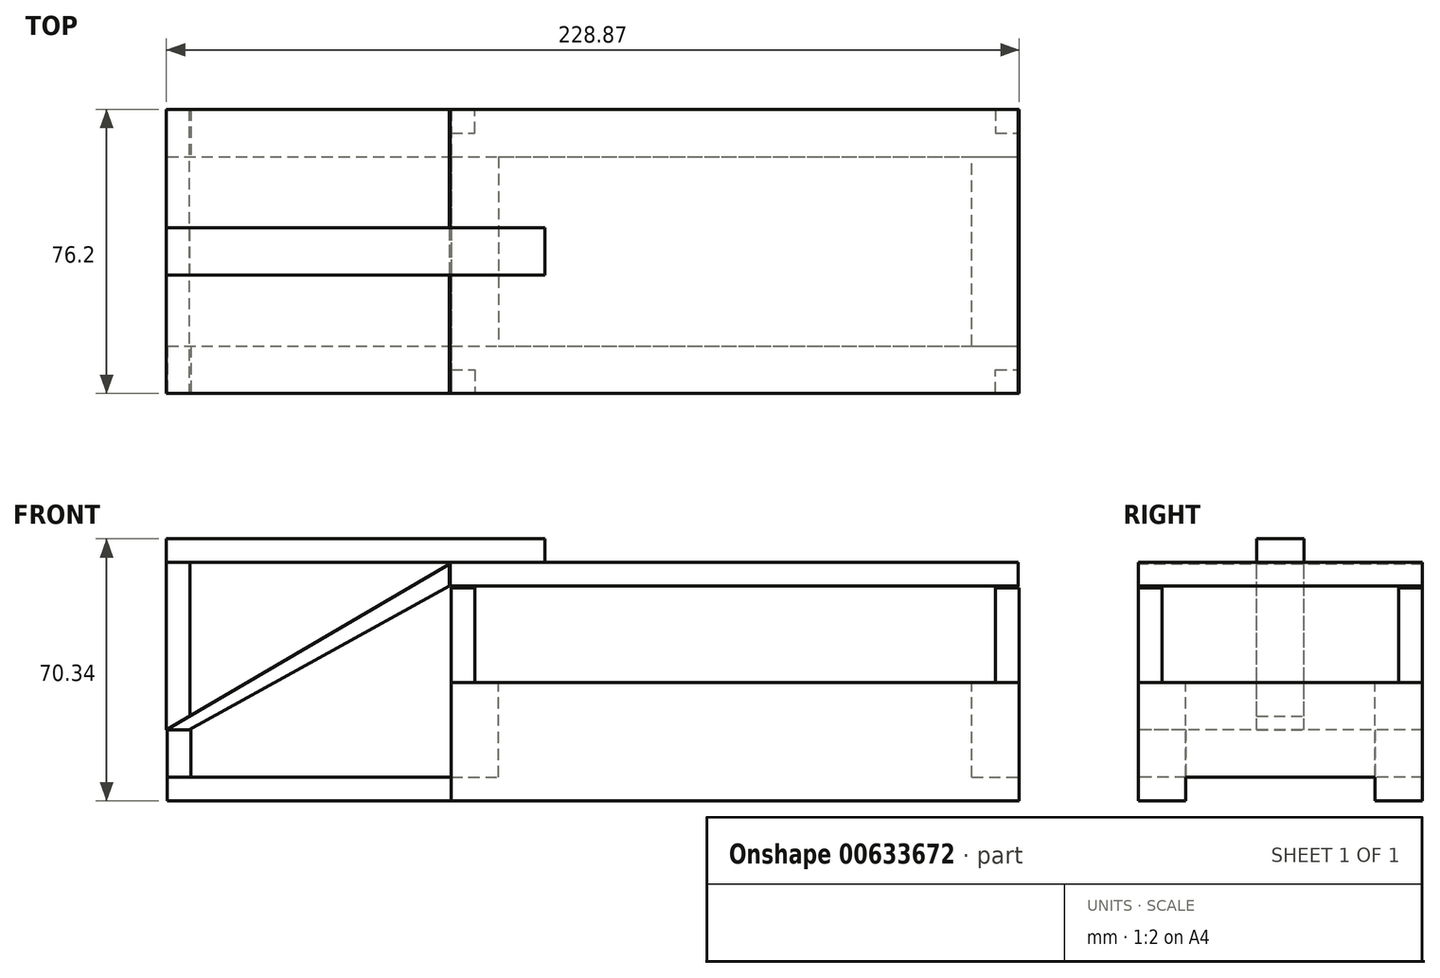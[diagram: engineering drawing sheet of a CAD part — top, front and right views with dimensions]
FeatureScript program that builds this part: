
annotation { "Feature Type Name" : "Feature", "Feature Type Description" : "" }
export const myFeature = defineFeature(function(context is Context, id is Id, definition is map)
    precondition{}
    {
        {
            var Q0;
            Q0=qCreatedBy(makeId("Front.planeOp"),FACE);
            var sketch = newSketch(context, id + "F0", { "sketchPlane" : qUnion([Q0])});
            skLineSegment(sketch, "E0", {"start": v(-114.8, -72) * mm, "end": v(37.6, -72) * mm});
            skLineSegment(sketch, "E1", {"start": v(37.6, -72) * mm, "end": v(37.6, -40.25) * mm});
            skLineSegment(sketch, "E2", {"start": v(37.6, -40.25) * mm, "end": v(-114.8, -40.25) * mm});
            skLineSegment(sketch, "E3", {"start": v(-114.8, -40.25) * mm, "end": v(-114.8, -72) * mm});
            skLineSegment(sketch, "E4", {"start": v(-114.8, -65.65) * mm, "end": v(37.6, -65.65) * mm});
            skSolve(sketch);
        }
        {
            var Q0;
            Q0 = qSketchRegion(id + "F0", true);
            extrude(context, id + "F1", {"entities" : qUnion([Q0]), "oppositeDirection" : true, "depth" : 76.2 * mm, "offsetDistance" : 25.4 * mm});
        }
        {
            var Q0;
            Q0=makeQuery(id+"F1.opExtrude","SWEPT_FACE",FACE,{"disambiguationData":[OSD([sQuery(id+"F0.wireOp",EDGE,"E2")])]});
            var sketch = newSketch(context, id + "F2", { "sketchPlane" : qUnion([Q0])});
            skLineSegment(sketch, "E5", {"start": v(-114.8, 69.85) * mm, "end": v(-108.44, 69.85) * mm});
            skLineSegment(sketch, "E6", {"start": v(-108.44, 69.85) * mm, "end": v(-108.44, 76.2) * mm});
            skLineSegment(sketch, "E7", {"start": v(-114.8, 6.35) * mm, "end": v(-108.44, 6.35) * mm});
            skLineSegment(sketch, "E8", {"start": v(-108.44, 6.35) * mm, "end": v(-108.44, 0) * mm});
            skLineSegment(sketch, "E9", {"start": v(31.26, 76.2) * mm, "end": v(31.26, 69.85) * mm});
            skLineSegment(sketch, "E10", {"start": v(31.26, 69.85) * mm, "end": v(37.6, 69.85) * mm});
            skLineSegment(sketch, "E11", {"start": v(31.26, 0) * mm, "end": v(31.26, 6.35) * mm});
            skLineSegment(sketch, "E12", {"start": v(31.26, 6.35) * mm, "end": v(37.6, 6.35) * mm});
            skSolve(sketch);
        }
        {
            var Q0;
            Q0 = qSketchRegion(id + "F2", true);
            var Q1;
            {var subQ0=sQuery(id+"F2.wireOp",EDGE,"E5");Q1=makeQuery(id+"F2.imprint","IMPRINT",FACE,{"disambiguationData":[TD([[makeQuery(id+"F2.imprint","IMPRINT",EDGE,{"derivedFrom":subQ0}),1.0]])]});}
            extrude(context, id + "F3", {"entities" : qUnion([Q0, Q1]), "depth" : 25.4 * mm, "offsetDistance" : 25.4 * mm});
        }
        {
            var Q0;
            {var subQ0=sQuery(id+"F2.wireOp",EDGE,"E7");Q0=makeQuery(id+"F2.imprint","IMPRINT",FACE,{"disambiguationData":[TD([[makeQuery(id+"F2.imprint","IMPRINT",EDGE,{"derivedFrom":subQ0}),-1.0]])]});}
            extrude(context, id + "F4", {"entities" : qUnion([Q0]), "depth" : 25.4 * mm, "offsetDistance" : 25.4 * mm});
        }
        {
            var Q0;
            {var subQ0=sQuery(id+"F2.wireOp",EDGE,"E11");Q0=makeQuery(id+"F2.imprint","IMPRINT",FACE,{"disambiguationData":[TD([[makeQuery(id+"F2.imprint","IMPRINT",EDGE,{"derivedFrom":subQ0}),-1.0]])]});}
            extrude(context, id + "F5", {"entities" : qUnion([Q0]), "depth" : 25.4 * mm, "offsetDistance" : 25.4 * mm});
        }
        {
            var Q0;
            {var subQ0=sQuery(id+"F2.wireOp",EDGE,"E9");Q0=makeQuery(id+"F2.imprint","IMPRINT",FACE,{"disambiguationData":[TD([[makeQuery(id+"F2.imprint","IMPRINT",EDGE,{"derivedFrom":subQ0}),1.0]])]});}
            extrude(context, id + "F6", {"entities" : qUnion([Q0]), "depth" : 25.4 * mm, "offsetDistance" : 25.4 * mm});
        }
        {
            var Q0;
            {var subQ0=sQuery(id+"F0.wireOp",EDGE,"E2");var subQ1=sQuery(id+"F0.wireOp",EDGE,"E1");Q0=makeQuery(id+"F6.boolean.opBoolean","MERGE",FACE,{"derivedFrom":[makeQuery(id+"F5.boolean.opBoolean","MERGE",FACE,{"derivedFrom":[makeQuery(id+"F1.opExtrude","SWEPT_FACE",FACE,{"disambiguationData":[OSD([subQ1])]}),makeQuery(id+"F5.opExtrude","SWEPT_FACE",FACE,{"disambiguationData":[OSD([subQ1,subQ0])]})]}),makeQuery(id+"F6.opExtrude","SWEPT_FACE",FACE,{"disambiguationData":[OSD([subQ1,subQ0])]})]});}
            var sketch = newSketch(context, id + "F7", { "sketchPlane" : qUnion([Q0])});
            skLineSegment(sketch, "E13", {"start": v(12.7, -72) * mm, "end": v(12.7, -65.65) * mm});
            skLineSegment(sketch, "E14", {"start": v(12.7, -65.65) * mm, "end": v(63.5, -65.65) * mm});
            skLineSegment(sketch, "E15", {"start": v(63.5, -65.65) * mm, "end": v(63.5, -72) * mm});
            skSolve(sketch);
        }
        {
            var Q0;
            Q0 = qSketchRegion(id + "F7", true);
            var Q1;
            {var subQ0=sQuery(id+"F7.wireOp",EDGE,"E13");Q1=makeQuery(id+"F7.imprint","IMPRINT",FACE,{"disambiguationData":[TD([[makeQuery(id+"F7.imprint","IMPRINT",EDGE,{"derivedFrom":subQ0}),-1.0]])]});}
            extrude(context, id + "F8", {"entities" : qUnion([Q0, Q1]), "operationType" : NewBodyOperationType.REMOVE, "oppositeDirection" : true, "depth" : 155.96 * mm, "offsetDistance" : 25.4 * mm});
        }
        {
            var Q0;
            Q0=makeQuery(id+"F1.opExtrude","SWEPT_FACE",FACE,{"disambiguationData":[OSD([sQuery(id+"F0.wireOp",EDGE,"E2")])]});
            var sketch = newSketch(context, id + "F9", { "sketchPlane" : qUnion([Q0])});
            skLineSegment(sketch, "E16", {"start": v(-102.1, 63.5) * mm, "end": v(-102.1, 12.7) * mm});
            skLineSegment(sketch, "E17", {"start": v(-102.1, 12.7) * mm, "end": v(24.9, 12.7) * mm});
            skLineSegment(sketch, "E18", {"start": v(24.9, 12.7) * mm, "end": v(24.9, 63.5) * mm});
            skLineSegment(sketch, "E19", {"start": v(-102.1, 63.5) * mm, "end": v(24.9, 63.5) * mm});
            skSolve(sketch);
        }
        {
            var Q0;
            Q0 = qSketchRegion(id + "F9", true);
            extrude(context, id + "F10", {"entities" : qUnion([Q0]), "operationType" : NewBodyOperationType.REMOVE, "oppositeDirection" : true, "depth" : 44.7 * mm, "offsetDistance" : 25.4 * mm});
        }
        {
            var Q0;
            Q0=qCreatedBy(makeId("Front.planeOp"),FACE);
            var sketch = newSketch(context, id + "F11", { "sketchPlane" : qUnion([Q0])});
            skLineSegment(sketch, "E20", {"start": v(-115.05, -14.36) * mm, "end": v(37.35, -14.36) * mm});
            skLineSegment(sketch, "E21", {"start": v(37.35, -14.36) * mm, "end": v(37.35, -8) * mm});
            skLineSegment(sketch, "E22", {"start": v(37.35, -8) * mm, "end": v(-115.05, -8) * mm});
            skLineSegment(sketch, "E23", {"start": v(-115.05, -8) * mm, "end": v(-115.05, -14.36) * mm});
            skSolve(sketch);
        }
        {
            var Q0;
            Q0 = qSketchRegion(id + "F11", true);
            extrude(context, id + "F12", {"entities" : qUnion([Q0]), "oppositeDirection" : true, "depth" : 76.2 * mm, "offsetDistance" : 25.4 * mm});
        }
        {
            var Q0;
            Q0=makeQuery(id+"F12.opExtrude","SWEPT_FACE",FACE,{"disambiguationData":[OSD([sQuery(id+"F11.wireOp",EDGE,"E22")])]});
            var sketch = newSketch(context, id + "F13", { "sketchPlane" : qUnion([Q0])});
            skLineSegment(sketch, "E24", {"start": v(-89.65, 44.45) * mm, "end": v(-89.65, 31.75) * mm});
            skLineSegment(sketch, "E25", {"start": v(-89.65, 31.75) * mm, "end": v(-191.25, 31.75) * mm});
            skLineSegment(sketch, "E26", {"start": v(-89.65, 44.45) * mm, "end": v(-191.25, 44.45) * mm});
            skLineSegment(sketch, "E27", {"start": v(-191.25, 44.45) * mm, "end": v(-191.25, 31.75) * mm});
            skSolve(sketch);
        }
        {
            var Q0;
            Q0 = qSketchRegion(id + "F13", true);
            extrude(context, id + "F14", {"entities" : qUnion([Q0]), "depth" : 6.35 * mm, "offsetDistance" : 25.4 * mm});
        }
        {
            var Q0;
            Q0=makeQuery(id+"F1.opExtrude","SWEPT_FACE",FACE,{"disambiguationData":[OSD([sQuery(id+"F0.wireOp",EDGE,"E3")])]});
            var sketch = newSketch(context, id + "F15", { "sketchPlane" : qUnion([Q0])});
            skLineSegment(sketch, "E28", {"start": v(-12.7, -65.65) * mm, "end": v(0, -65.65) * mm});
            skSolve(sketch);
        }
        {
            var Q0;
            Q0 = qSketchRegion(id + "F15", true);
            var Q1;
            {var subQ0=sQuery(id+"F15.wireOp",EDGE,"E28");Q1=makeQuery(id+"F15.imprint","IMPRINT",FACE,{"disambiguationData":[TD([[makeQuery(id+"F15.imprint","IMPRINT",EDGE,{"derivedFrom":subQ0}),-1.0]])]});}
            extrude(context, id + "F16", {"entities" : qUnion([Q0, Q1]), "depth" : 76.2 * mm, "offsetDistance" : 25.4 * mm});
        }
        {
            var Q0;
            Q0=makeQuery(id+"F1.opExtrude","SWEPT_FACE",FACE,{"disambiguationData":[OSD([sQuery(id+"F0.wireOp",EDGE,"E3")])]});
            var sketch = newSketch(context, id + "F17", { "sketchPlane" : qUnion([Q0])});
            skLineSegment(sketch, "E29", {"start": v(-63.5, -65.65) * mm, "end": v(-76.2, -65.65) * mm});
            skSolve(sketch);
        }
        {
            var Q0;
            Q0 = qSketchRegion(id + "F17", true);
            var Q1;
            {var subQ0=sQuery(id+"F17.wireOp",EDGE,"E29");Q1=makeQuery(id+"F17.imprint","IMPRINT",FACE,{"disambiguationData":[TD([[makeQuery(id+"F17.imprint","IMPRINT",EDGE,{"derivedFrom":subQ0}),1.0]])]});}
            extrude(context, id + "F18", {"entities" : qUnion([Q0, Q1]), "depth" : 76.2 * mm, "offsetDistance" : 25.4 * mm});
        }
        {
            var Q0;
            Q0=makeQuery(id+"F18.opExtrude","SWEPT_FACE",FACE,{"disambiguationData":[OSD([sQuery(id+"F17.wireOp",EDGE,"E29")])]});
            var sketch = newSketch(context, id + "F19", { "sketchPlane" : qUnion([Q0])});
            skLineSegment(sketch, "E30", {"start": v(-184.64, 76.2) * mm, "end": v(-184.64, 63.5) * mm});
            skSolve(sketch);
        }
        {
            var Q0;
            Q0 = qSketchRegion(id + "F19", true);
            var Q1;
            {var subQ0=sQuery(id+"F19.wireOp",EDGE,"E30");Q1=makeQuery(id+"F19.imprint","IMPRINT",FACE,{"disambiguationData":[TD([[makeQuery(id+"F19.imprint","IMPRINT",EDGE,{"derivedFrom":subQ0}),-1.0]])]});}
            extrude(context, id + "F20", {"entities" : qUnion([Q0, Q1]), "depth" : 12.7 * mm, "offsetDistance" : 25.4 * mm});
        }
        {
            var Q0;
            Q0=makeQuery(id+"F16.opExtrude","SWEPT_FACE",FACE,{"disambiguationData":[OSD([sQuery(id+"F15.wireOp",EDGE,"E28")])]});
            var sketch = newSketch(context, id + "F21", { "sketchPlane" : qUnion([Q0])});
            skLineSegment(sketch, "E31", {"start": v(-184.64, 12.7) * mm, "end": v(-184.64, 0) * mm});
            skSolve(sketch);
        }
        {
            var Q0;
            Q0 = qSketchRegion(id + "F21", true);
            var Q1;
            {var subQ0=sQuery(id+"F21.wireOp",EDGE,"E31");Q1=makeQuery(id+"F21.imprint","IMPRINT",FACE,{"disambiguationData":[TD([[makeQuery(id+"F21.imprint","IMPRINT",EDGE,{"derivedFrom":subQ0}),-1.0]])]});}
            extrude(context, id + "F22", {"entities" : qUnion([Q0, Q1]), "depth" : 12.7 * mm, "offsetDistance" : 25.4 * mm});
        }
        {
            var Q0;
            Q0=qCreatedBy(makeId("Front.planeOp"),FACE);
            var sketch = newSketch(context, id + "F23", { "sketchPlane" : qUnion([Q0])});
            skLineSegment(sketch, "E32", {"start": v(-191.26, -52.96) * mm, "end": v(-185.16, -52.96) * mm});
            skLineSegment(sketch, "E33", {"start": v(-185.16, -52.96) * mm, "end": v(-115.31, -14.35) * mm});
            skLineSegment(sketch, "E34", {"start": v(-115.31, -14.35) * mm, "end": v(-115.31, -8.5) * mm});
            skLineSegment(sketch, "E35", {"start": v(-115.31, -8.5) * mm, "end": v(-191.26, -52.96) * mm});
            skSolve(sketch);
        }
        {
            var Q0;
            Q0 = qSketchRegion(id + "F23", true);
            extrude(context, id + "F24", {"entities" : qUnion([Q0]), "oppositeDirection" : true, "depth" : 76.2 * mm, "offsetDistance" : 25.4 * mm});
        }
        {
            var Q0;
            Q0=qCreatedBy(makeId("Front.planeOp"),FACE);
            var sketch = newSketch(context, id + "F25", { "sketchPlane" : qUnion([Q0])});
            skLineSegment(sketch, "E36", {"start": v(-191.02, -8.26) * mm, "end": v(-191.02, -52.96) * mm});
            skLineSegment(sketch, "E37", {"start": v(-184.67, -48.39) * mm, "end": v(-184.67, -8.26) * mm});
            skLineSegment(sketch, "E38", {"start": v(-184.67, -8.26) * mm, "end": v(-191.02, -8.26) * mm});
            skLineSegment(sketch, "E39", {"start": v(-191.02, -52.96) * mm, "end": v(-184.67, -48.39) * mm});
            skSolve(sketch);
        }
        {
            var Q0;
            Q0 = qSketchRegion(id + "F25", true);
            extrude(context, id + "F26", {"entities" : qUnion([Q0]), "oppositeDirection" : true, "depth" : 44.45 * mm, "offsetDistance" : 25.4 * mm});
        }
        {
            var Q0;
            Q0=makeQuery(id+"F26.opExtrude","SWEPT_BODY",BODY,{"disambiguationData":[OSD([sQuery(id+"F25.wireOp",EDGE,"E36"),sQuery(id+"F25.wireOp",EDGE,"E37"),sQuery(id+"F25.wireOp",EDGE,"E38"),sQuery(id+"F25.wireOp",EDGE,"E39")])]});
            deleteBodies(context, id + "F27", {"entities" : qUnion([Q0])});
        }
        {
            var Q0;
            Q0=makeQuery(id+"F14.opExtrude","CAP_FACE",FACE,{"disambiguationData":[OSD([sQuery(id+"F13.wireOp",EDGE,"E24"),sQuery(id+"F13.wireOp",EDGE,"E25"),sQuery(id+"F13.wireOp",EDGE,"E26"),sQuery(id+"F13.wireOp",EDGE,"E27")])],"isStart":true});
            var sketch = newSketch(context, id + "F28", { "sketchPlane" : qUnion([Q0])});
            skLineSegment(sketch, "E40.bottom", {"start": v(-191.25, -44.45) * mm, "end": v(-184.9, -44.45) * mm});
            skLineSegment(sketch, "E40.top", {"start": v(-191.25, -31.75) * mm, "end": v(-184.9, -31.75) * mm});
            skLineSegment(sketch, "E40.left", {"start": v(-191.25, -44.45) * mm, "end": v(-191.25, -31.75) * mm});
            skLineSegment(sketch, "E40.right", {"start": v(-184.9, -44.45) * mm, "end": v(-184.9, -31.75) * mm});
            skSolve(sketch);
        }
        {
            var Q0;
            Q0 = qSketchRegion(id + "F28", true);
            extrude(context, id + "F29", {"entities" : qUnion([Q0]), "endBound" : BoundingType.UP_TO_NEXT, "depth" : 25.4 * mm, "offsetDistance" : 25.4 * mm});
        }
    });
